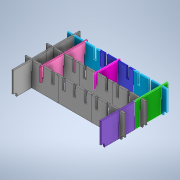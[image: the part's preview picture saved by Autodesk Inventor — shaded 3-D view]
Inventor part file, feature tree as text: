
AUTODESK INVENTOR PART (.ipt)
format: ipt  version: 2022 (Build 260153000, 153)  size: 2,030,080 bytes
history: native  units: mm
features: other x21, extrude x21, sketch x21, fillet x20, pattern_linear x2, mirror x2
ambient origin geometry x8: Origin, YZ Plane, XZ Plane, XY Plane, X Axis, Y Axis, Z Axis, Center Point
bodies: Solid13 (feature_tree), Solid16 (feature_tree), Solid19 (feature_tree), Solid15 (feature_tree), Solid18 (feature_tree), Solid14 (feature_tree), Solid17 (feature_tree), Solid20 (feature_tree), Solid21 (feature_tree)
feature tree (87):
  other  "Flightcase Interior"
  other  "Annotations"
  extrude  "Extrusion1"  Depth=289.0mm
  extrude  "Extrusion2"  Depth=214.5mm
  fillet  "Fillet1"  Radius=9.0mm
  extrude  "Extrusion10"  Depth=9.0mm
  extrude  "Extrusion11"  Depth=23.0mm
  extrude  "Extrusion14"  Depth=108.0mm TaperAngle=0.0deg
  extrude  "Extrusion12"  Depth=20.0mm TaperAngle=0.0deg
  extrude  "Extrusion13"  Depth=15.0mm
  pattern_linear  "Rectangular Pattern1"  Spacing1=5.0mm  [1 undecoded]
  fillet  "Fillet15"  Radius=10.0mm
  fillet  "Fillet2"  Radius=15.0mm
  fillet  "Fillet3"  Radius=10.0mm
  fillet  "Fillet16"  Radius=60.0mm
  fillet  "Fillet4"  Radius=2.0mm
  fillet  "Fillet5"  Radius=2.0mm
  fillet  "Fillet6"  Radius=2.0mm
  fillet  "Fillet7"  Radius=1.5mm
  mirror  "Mirror3"
  extrude  "Extrusion15"  Depth=15.0mm
  extrude  "Extrusion16"  Depth=15.0mm
  extrude  "Extrusion17"  Depth=15.0mm TaperAngle=0.0deg
  extrude  "Extrusion18"  Depth=15.0mm
  extrude  "Extrusion19"  Depth=15.0mm TaperAngle=0.0deg
  extrude  "Extrusion20"  Depth=15.0mm
  fillet  "Fillet8"  Radius=2.0mm
  extrude  "Extrusion21"  Depth=15.0mm
  fillet  "Fillet9"  Radius=1.5mm
  extrude  "Extrusion22"  Depth=15.0mm
  fillet  "Fillet10"  Radius=61.0mm
  fillet  "Fillet11"  Radius=15.0mm
  fillet  "Fillet12"  Radius=10.0mm
  fillet  "Fillet13"  Radius=15.0mm
  fillet  "Fillet14"  Radius=10.0mm
  fillet  "Fillet17"  Radius=15.0mm
  fillet  "Fillet18"  Radius=2.0mm
  pattern_linear  "Rectangular Pattern2"  Spacing1=15.0mm  [1 undecoded]
  mirror  "Mirror4"
  extrude  "Extrusion23"  Depth=15.0mm TaperAngle=0.0deg
  extrude  "Extrusion24"  Depth=15.0mm
  extrude  "Extrusion25"  Depth=15.0mm
  extrude  "Extrusion26"  Depth=15.0mm
  extrude  "Extrusion27"  Depth=15.0mm
  extrude  "Extrusion28"  Depth=15.0mm TaperAngle=0.0deg
  fillet  "Fillet19"  Radius=7.0mm
  fillet  "Fillet20"  Radius=2.0mm
  sketch  "Sketch1"  dims[d0=429.0mm d1=289.0mm]
  sketch  "Sketch2"  dims[d2=144.5mm d3=214.5mm d4=9.0mm]
  sketch  "Sketch10"  dims[d5=9.0mm d6=9.0mm]
  other  "PART_A_hoz"
  sketch  "Sketch11"  dims[d7=9.0mm d8=23.0mm]
  sketch  "Sketch13"  dims[d9=27.0mm d10=108.0mm d11=0.0mm]
  sketch  "Sketch14"  dims[d21=27.0mm d23=20.0mm d24=0.0mm]
  other  "PART_B_hoz"
  sketch  "Sketch15"  dims[d25=15.0mm d38=7.0mm]
  sketch  "Sketch16"  dims[d120=143.0mm d125=15.0mm]
  other  "PART_C_vert"
  sketch  "Sketch17"  dims[d172=7.0mm]
  sketch  "Sketch18"  dims[d173=2.0mm]
  sketch  "Sketch19"  dims[d174=143.0mm d175=0.0mm]
  other  "PART_D_vert"
  sketch  "Sketch21"  dims[d176=7.0mm]
  sketch  "Sketch22"  dims[d177=45.0mm d178=0.0mm]
  other  "Pattern of PART_A_hoz:3"
  sketch  "Sketch24"  dims[d179=1.5mm]
  sketch  "Sketch25"  dims[d181=2.0mm]
  other  "Pattern of Solid13:4"
  other  "Pattern of Solid13:5"
  other  "Pattern of PART_B_hoz:6"
  other  "Pattern of PART_B_hoz:7"
  other  "Pattern of PART_A_hoz:8"
  other  "Pattern of PART_A_hoz:9"
  other  "Pattern of PART_C_vert:10"
  other  "Pattern of PART_D_vert:11"
  sketch  "Sketch26"  dims[d182=1.5mm]
  other  "PART_F_2waydiv"
  sketch  "Sketch28"  dims[d183=2.0mm]
  sketch  "Sketch29"  dims[d184=5.0mm]
  sketch  "Sketch30"  dims[d185=45.0mm d186=0.0mm]
  other  "PART_E_div"
  sketch  "Sketch31"  dims[d187=143.0mm]
  sketch  "Sketch32"  dims[d188=143.0mm d190=5.0mm d191=10.0mm d192=0.0mm d193=15.0mm d194=10.0mm d195=0.0mm d196=60.0mm d198=47.0mm d199=2.0mm d200=2.0mm d201=2.0mm d202=1.5mm d203=1.5mm d204=1.5mm d205=144.5mm d206=0.0mm d207=15.0mm d208=144.5mm d209=0.0mm d210=2.0mm d211=2.0mm d212=1.5mm d213=1.5mm d214=5.0mm d215=61.0mm d216=0.0mm d217=15.0mm d218=10.0mm d219=0.0mm d220=15.0mm d221=10.0mm d222=0.0mm d223=15.0mm d224=0.0mm d225=2.0mm d226=15.0mm d227=10.0mm d228=0.0mm d229=2.0mm d231=7.0mm d232=7.0mm d235=90.0mm d236=90.0mm d238=10.0mm d239=0.0mm d240=7.0mm d241=2.0mm d244=90.0mm d245=7.0mm d246=2.0mm d247=2.0mm d248=7.0mm d249=2.0mm d250=1.5mm d251=1.5mm d252=30.0mm d254=90.0mm d255=7.0mm d256=7.0mm d259=10.0mm d260=0.0mm d261=10.0mm d262=0.0mm d263=15.0mm d264=0.0mm d265=7.0mm d266=7.0mm d267=7.0mm d268=15.0mm d269=0.0mm d270=10.0mm d271=0.0mm d272=10.0mm d273=0.0mm d274=2.0mm d275=2.0mm d26=2.832357mm d27=8.593144mm d28=429.0mm d29=2.489469mm d30=6.513538mm d31=289.0mm d32=108.0mm]
  other  "General Note 1"
  other  "Linear Dimension 1"
  other  "Linear Dimension 2"
  other  "Linear Dimension 3"
note: 2 required parameter values undecoded (feature->parameter linkage not recoverable at this tier; creation-order binding heuristic only, values carry confidence <= 0.55)
